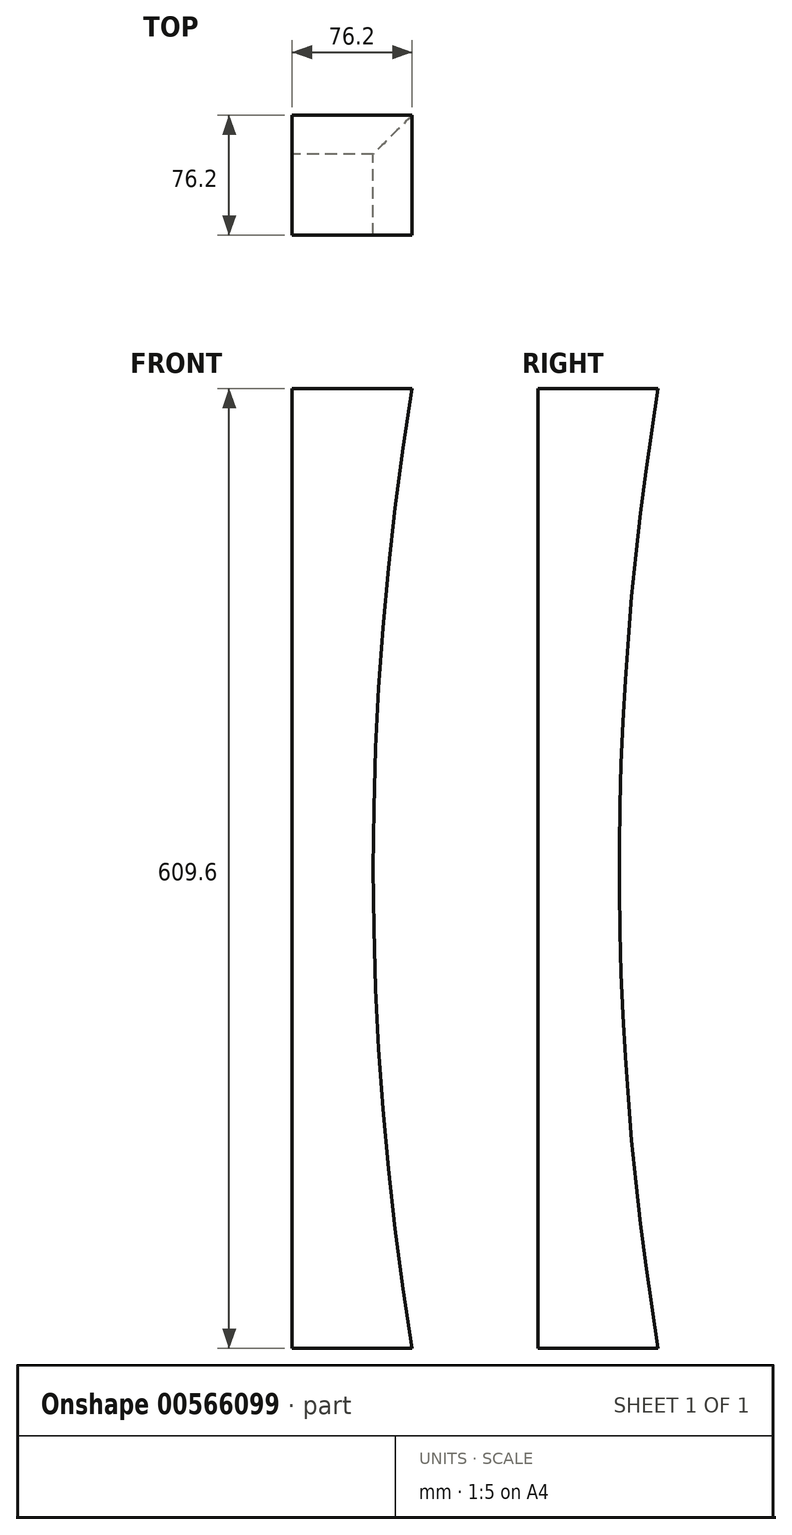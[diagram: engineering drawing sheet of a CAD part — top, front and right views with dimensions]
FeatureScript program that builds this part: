
annotation { "Feature Type Name" : "Feature", "Feature Type Description" : "" }
export const myFeature = defineFeature(function(context is Context, id is Id, definition is map)
    precondition{}
    {
        {
            var Q0;
            Q0=qCreatedBy(makeId("Top.planeOp"),FACE);
            var sketch = newSketch(context, id + "F0", { "sketchPlane" : qUnion([Q0])});
            skLineSegment(sketch, "E0.bottom", {"start": v(0, 0) * mm, "end": v(76.2, 0) * mm});
            skLineSegment(sketch, "E0.top", {"start": v(0, 76.2) * mm, "end": v(76.2, 76.2) * mm});
            skLineSegment(sketch, "E0.left", {"start": v(0, 0) * mm, "end": v(0, 76.2) * mm});
            skLineSegment(sketch, "E0.right", {"start": v(76.2, 0) * mm, "end": v(76.2, 76.2) * mm});
            skSolve(sketch);
        }
        {
            var Q0;
            Q0 = qSketchRegion(id + "F0", true);
            extrude(context, id + "F1", {"entities" : qUnion([Q0]), "depth" : 609.6 * mm, "offsetDistance" : 25.4 * mm});
        }
        {
            var Q0;
            Q0=makeQuery(id+"F1.opExtrude","SWEPT_FACE",FACE,{"disambiguationData":[OSD([sQuery(id+"F0.wireOp",EDGE,"E0.bottom")])]});
            var sketch = newSketch(context, id + "F2", { "sketchPlane" : qUnion([Q0])});
            skArc(sketch, "E1", {"start": v(76.2, 609.63) * mm, "mid": v(51.46, 304.81) * mm, "end": v(76.2, 0) * mm});
            skSolve(sketch);
        }
        {
            var Q0;
            {var subQ1=sQuery(id+"F0.wireOp",EDGE,"E0.bottom");var subQ2=makeQuery(id+"F1.opExtrude","SWEPT_EDGE",EDGE,{"disambiguationData":[OSD([subQ1,sQuery(id+"F0.wireOp",EDGE,"E0.right")])]});Q0=makeQuery(id+"F2.imprint","IMPRINT",FACE,{"disambiguationData":[TD([[makeQuery(id+"F2.imprint","IMPRINT",EDGE,{"derivedFrom":subQ2}),-1.0]])]});}
            var Q1;
            Q1=makeQuery(id+"F1.opExtrude","CAP_EDGE",EDGE,{"disambiguationData":[OSD([sQuery(id+"F0.wireOp",EDGE,"E0.right")])],"isStart":false});
            var Q2;
            Q2=makeQuery(id+"F1.opExtrude","CAP_EDGE",EDGE,{"disambiguationData":[OSD([sQuery(id+"F0.wireOp",EDGE,"E0.top")])],"isStart":false});
            sweep(context, id + "F3", {"operationType" : NewBodyOperationType.REMOVE, "profiles" : qUnion([Q0]), "path" : qUnion([Q1, Q2])});
        }
    });
